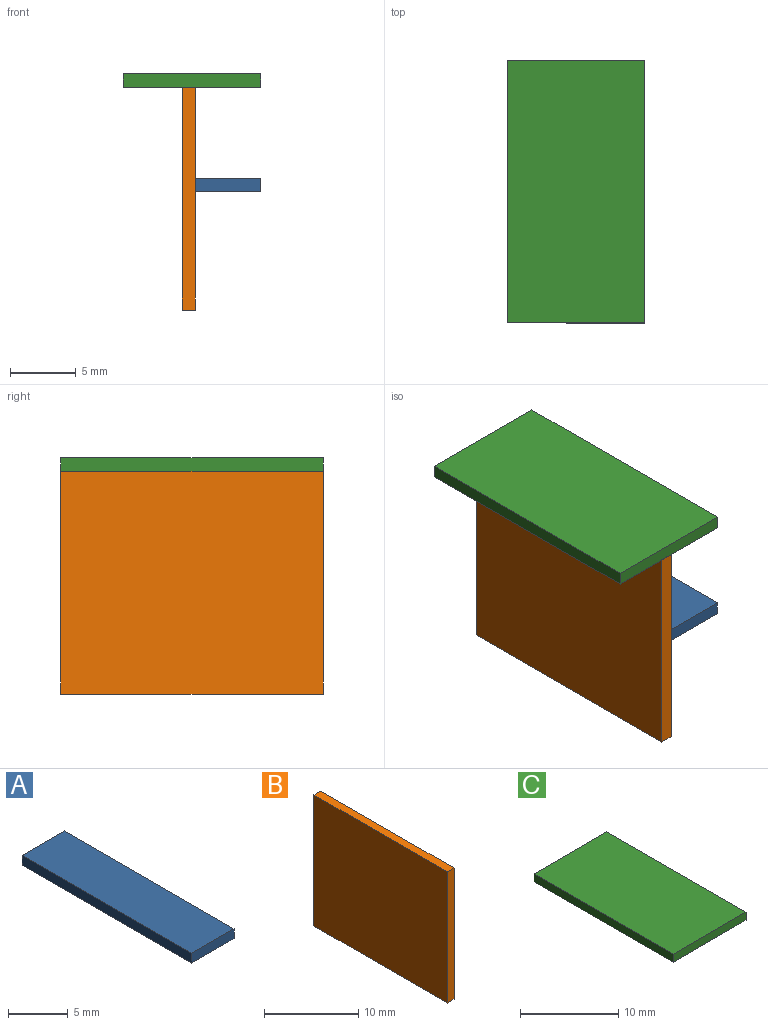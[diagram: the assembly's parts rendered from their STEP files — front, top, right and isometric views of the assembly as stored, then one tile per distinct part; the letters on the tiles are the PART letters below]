
ASSEMBLY  parts=3 mates=2
PART A: 6 faces, bbox 5x20x1 mm
  f0: plane 20x5mm, normal (0,0,1), area 100mm2, adj f1,f3,f4,f5
  f1: plane 20x1mm, normal (-1,0,0), area 20mm2, adj f0,f2,f4,f5
  f2: plane 20x5mm, normal (0,0,-1), area 100mm2, adj f1,f3,f4,f5
  f3: plane 20x1mm, normal (1,0,0), area 20mm2, adj f0,f2,f4,f5
  f4: plane 5x1mm, normal (0,-1,0), area 5mm2, adj f0,f1,f2,f3
  f5: plane 5x1mm, normal (0,1,0), area 5mm2, adj f0,f1,f2,f3
PART B: 6 faces, bbox 1x20x17 mm
  f0: plane 20x1mm, normal (0,0,1), area 20mm2, adj f1,f3,f4,f5
  f1: plane 20x17mm, normal (-1,0,0), area 340mm2, adj f0,f2,f4,f5
  f2: plane 20x1mm, normal (0,0,-1), area 20mm2, adj f1,f3,f4,f5
  f3: plane 20x17mm, normal (1,0,0), area 340mm2, adj f0,f2,f4,f5
  f4: plane 17x1mm, normal (0,-1,0), area 17mm2, adj f0,f1,f2,f3
  f5: plane 17x1mm, normal (0,1,0), area 17mm2, adj f0,f1,f2,f3
PART C: 6 faces, bbox 10.5x20x1 mm
  f0: plane 20x10.5mm, normal (0,0,1), area 210mm2, adj f1,f3,f4,f5
  f1: plane 20x1mm, normal (-1,0,0), area 20mm2, adj f0,f2,f4,f5
  f2: plane 20x10.5mm, normal (0,0,-1), area 210mm2, adj f1,f3,f4,f5
  f3: plane 20x1mm, normal (1,0,0), area 20mm2, adj f0,f2,f4,f5
  f4: plane 10.5x1mm, normal (0,-1,0), area 10.5mm2, adj f0,f1,f2,f3
  f5: plane 10.5x1mm, normal (0,1,0), area 10.5mm2, adj f0,f1,f2,f3
PLACE A t=(-31.32,8.55,-62.25)mm
PLACE B t=(-21.67,8.55,-63.34)mm
PLACE C t=(-19,8.55,-66.12)mm
MATE fastened A.f4 <-> B.f4  axis (0,-1,0) through (8.24,-11.45,-6.92)mm
MATE fastened B.f4 <-> C.f4  axis (0,-1,0) through (7.24,-11.45,0.08)mm
